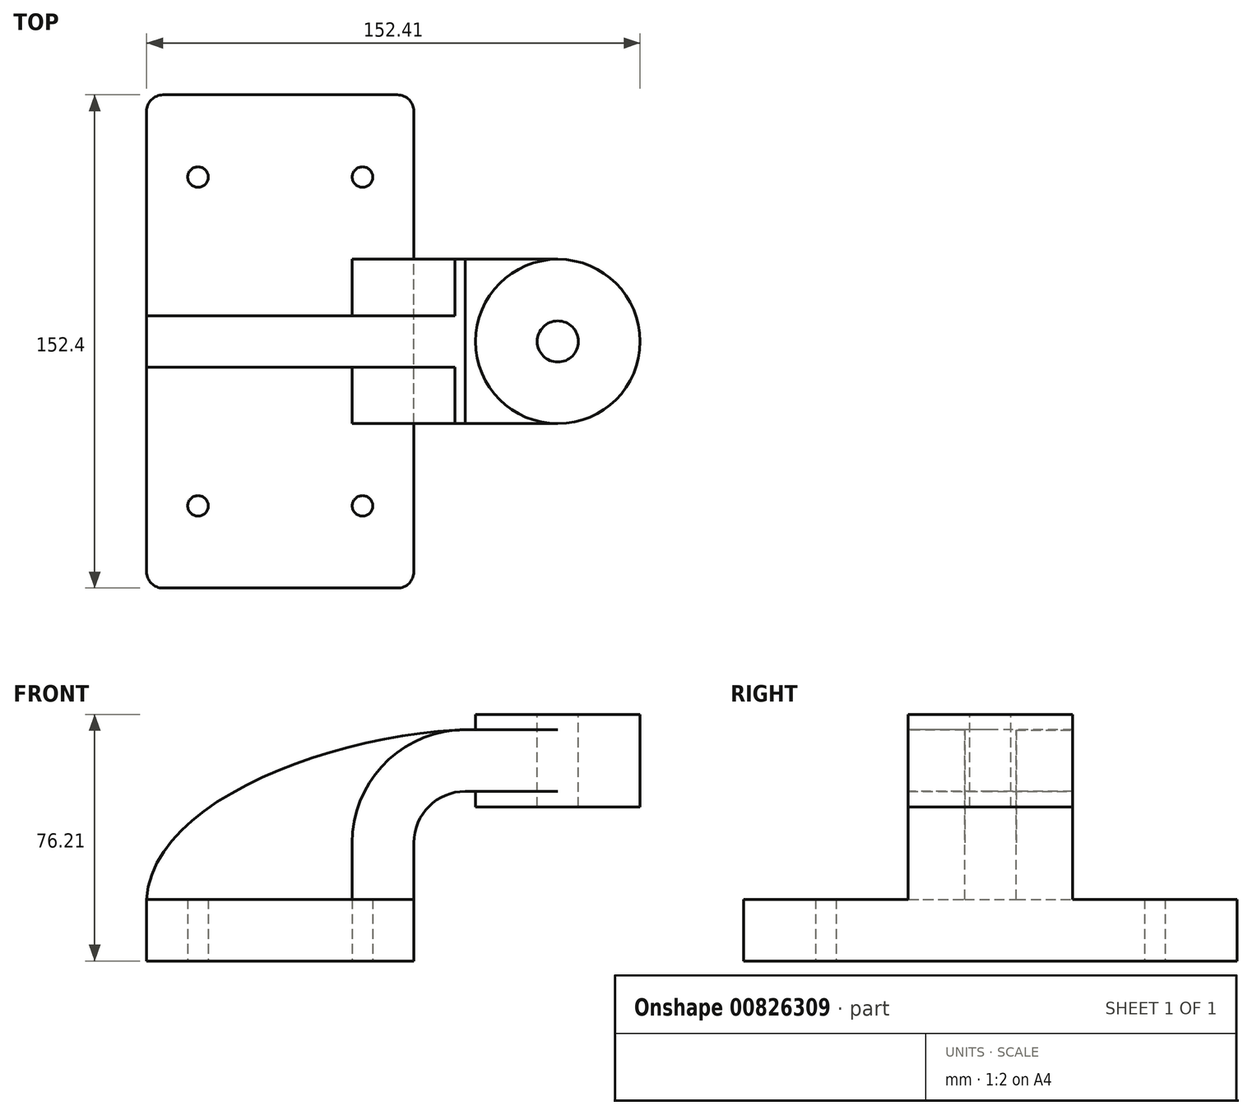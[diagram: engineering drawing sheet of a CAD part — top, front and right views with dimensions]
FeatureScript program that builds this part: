
annotation { "Feature Type Name" : "Feature", "Feature Type Description" : "" }
export const myFeature = defineFeature(function(context is Context, id is Id, definition is map)
    precondition{}
    {
        {
            var Q0;
            Q0=qCreatedBy(makeId("Front.planeOp"),FACE);
            var sketch = newSketch(context, id + "F0", { "sketchPlane" : qUnion([Q0])});
            skLineSegment(sketch, "E0.rect.bottom", {"start": v(-41.28, 9.52) * mm, "end": v(41.28, 9.52) * mm});
            skLineSegment(sketch, "E0.rect.top", {"start": v(-41.28, -9.52) * mm, "end": v(41.28, -9.52) * mm});
            skLineSegment(sketch, "E0.rect.left", {"start": v(-41.28, 9.52) * mm, "end": v(-41.28, -9.52) * mm});
            skLineSegment(sketch, "E0.rect.right", {"start": v(41.28, 9.52) * mm, "end": v(41.28, -9.52) * mm});
            skPoint(sketch, "E0.rect.middle", {"position": v(0, 0) * mm});
            skLineSegment(sketch, "E1", {"start": v(41.28, 9.52) * mm, "end": v(41.28, 27) * mm});
            skArc(sketch, "E2", {"start": v(41.28, 27) * mm, "mid": v(45.92, 38.23) * mm, "end": v(57.15, 42.88) * mm});
            skLineSegment(sketch, "E3", {"start": v(57.15, 42.88) * mm, "end": v(85.72, 42.88) * mm});
            skLineSegment(sketch, "E4.rect.bottom", {"start": v(60.32, 38.1) * mm, "end": v(111.12, 38.1) * mm});
            skLineSegment(sketch, "E4.rect.top", {"start": v(60.32, 66.68) * mm, "end": v(111.12, 66.68) * mm});
            skLineSegment(sketch, "E4.rect.left", {"start": v(60.32, 38.1) * mm, "end": v(60.32, 66.68) * mm});
            skLineSegment(sketch, "E4.rect.right", {"start": v(111.13, 38.1) * mm, "end": v(111.12, 66.68) * mm});
            skPoint(sketch, "E4.rect.middle", {"position": v(85.72, 52.39) * mm});
            skLineSegment(sketch, "E5.0", {"start": v(57.15, 61.93) * mm, "end": v(85.72, 61.93) * mm});
            skArc(sketch, "E5.1", {"start": v(22.23, 27) * mm, "mid": v(32.45, 51.7) * mm, "end": v(57.15, 61.93) * mm});
            skLineSegment(sketch, "E5.2", {"start": v(22.23, 9.52) * mm, "end": v(22.23, 27) * mm});
            skLineSegment(sketch, "E6", {"start": v(85.72, 38.1) * mm, "end": v(85.72, 66.68) * mm});
            skFitSpline(sketch, "E7", {"points": [v(-41.28, 9.53) * mm, v(57.15, 61.93) * mm], "startDerivative": vector(5.2, 92.34) * mm, "endDerivative": vector(120.92, 4.22) * mm});
            skSolve(sketch);
        }
        {
            var Q0;
            Q0=makeQuery(id+"F0.imprint","IMPRINT",FACE,{"disambiguationData":[TD([[makeQuery(id+"F0.imprint","IMPRINT",EDGE,{"derivedFrom":sQuery(id+"F0.wireOp",EDGE,"E0.rect.top")}),1.0]])]});
            extrude(context, id + "F1", {"entities" : qUnion([Q0]), "endBound" : BoundingType.SYMMETRIC, "depth" : 152.4 * mm, "offsetDistance" : 25.4 * mm});
        }
        {
            var Q0;
            {var subQ9=sQuery(id+"F0.wireOp",EDGE,"E1");Q0=makeQuery(id+"F0.imprint","IMPRINT",FACE,{"disambiguationData":[TD([[makeQuery(id+"F0.imprint","IMPRINT",EDGE,{"derivedFrom":subQ9}),1.0]])]});}
            var Q1;
            {var subQ0=sQuery(id+"F0.wireOp",EDGE,"E6");var subQ1=sQuery(id+"F0.wireOp",EDGE,"E3");var subQ2=makeQuery(id+"F0.imprint","INTERSECT",VERTEX,{"derivedFrom":[subQ1,subQ0]});Q1=makeQuery(id+"F0.imprint","IMPRINT",FACE,{"disambiguationData":[TD([[makeQuery(id+"F0.imprint","IMPRINT",EDGE,{"disambiguationData":[TD([[subQ2,1.0]])],"derivedFrom":subQ1}),1.0]])]});}
            extrude(context, id + "F2", {"entities" : qUnion([Q0, Q1]), "operationType" : NewBodyOperationType.ADD, "endBound" : BoundingType.SYMMETRIC, "depth" : 50.8 * mm});
        }
        {
            var Q0;
            {var subQ3=sQuery(id+"F0.wireOp",EDGE,"E5.2");Q0=makeQuery(id+"F0.imprint","IMPRINT",FACE,{"disambiguationData":[TD([[makeQuery(id+"F0.imprint","IMPRINT",EDGE,{"derivedFrom":subQ3}),1.0]])]});}
            extrude(context, id + "F3", {"entities" : qUnion([Q0]), "operationType" : NewBodyOperationType.ADD, "endBound" : BoundingType.SYMMETRIC, "depth" : 15.88 * mm});
        }
        {
            var Q0;
            {var subQ5=sQuery(id+"F0.wireOp",EDGE,"E4.rect.right");Q0=makeQuery(id+"F0.imprint","IMPRINT",FACE,{"disambiguationData":[TD([[makeQuery(id+"F0.imprint","IMPRINT",EDGE,{"derivedFrom":subQ5}),1.0]])]});}
            var Q1;
            Q1=sQuery(id+"F0.wireOp",EDGE,"E6");
            revolve(context, id + "F4", {"operationType" : NewBodyOperationType.ADD, "entities" : qUnion([Q0]), "axis" : qUnion([Q1]), "revolveType" : RevolveType.FULL});
        }
        {
            var Q0;
            Q0=makeQuery(id+"F1.opExtrude","CAP_EDGE",EDGE,{"disambiguationData":[OSD([sQuery(id+"F0.wireOp",EDGE,"E0.rect.right")])],"isStart":false});
            var Q1;
            Q1=makeQuery(id+"F1.opExtrude","CAP_EDGE",EDGE,{"disambiguationData":[OSD([sQuery(id+"F0.wireOp",EDGE,"E0.rect.left")])],"isStart":false});
            var Q2;
            Q2=makeQuery(id+"F1.opExtrude","CAP_EDGE",EDGE,{"disambiguationData":[OSD([sQuery(id+"F0.wireOp",EDGE,"E0.rect.right")])],"isStart":true});
            var Q3;
            Q3=makeQuery(id+"F1.opExtrude","CAP_EDGE",EDGE,{"disambiguationData":[OSD([sQuery(id+"F0.wireOp",EDGE,"E0.rect.left")])],"isStart":true});
            fillet(context, id + "F5", {"entities" : qUnion([Q0, Q1, Q2, Q3]), "radius" : 5.08 * mm, "tangentPropagation" : true, "allowEdgeOverflow" : false});
        }
        {
            var Q0;
            Q0=makeQuery(id+"F4.opRevolve","SWEPT_FACE",FACE,{"disambiguationData":[OSD([sQuery(id+"F0.wireOp",EDGE,"E4.rect.top")])]});
            var sketch = newSketch(context, id + "F6", { "sketchPlane" : qUnion([Q0])});
            skCircle(sketch, "E8", {"center": v(85.72, 0) * mm, "radius": 6.35 * mm});
            skSolve(sketch);
        }
        {
            var Q0;
            Q0 = qSketchRegion(id + "F6", true);
            extrude(context, id + "F7", {"entities" : qUnion([Q0]), "operationType" : NewBodyOperationType.REMOVE, "oppositeDirection" : true, "depth" : 70.61 * mm, "offsetDistance" : 25.4 * mm});
        }
        {
            var Q0;
            Q0=makeQuery(id+"F1.opExtrude","SWEPT_FACE",FACE,{"disambiguationData":[OSD([sQuery(id+"F0.wireOp",EDGE,"E0.rect.top")])]});
            var sketch = newSketch(context, id + "F8", { "sketchPlane" : qUnion([Q0])});
            skCircle(sketch, "E9", {"center": v(25.4, -50.8) * mm, "radius": 3.18 * mm});
            skCircle(sketch, "E10", {"center": v(-25.4, -50.8) * mm, "radius": 3.18 * mm});
            skCircle(sketch, "E11", {"center": v(-25.4, 50.8) * mm, "radius": 3.18 * mm});
            skCircle(sketch, "E12", {"center": v(25.4, 50.8) * mm, "radius": 3.18 * mm});
            skSolve(sketch);
        }
        {
            var Q0;
            Q0 = qSketchRegion(id + "F8", true);
            extrude(context, id + "F9", {"entities" : qUnion([Q0]), "operationType" : NewBodyOperationType.REMOVE, "oppositeDirection" : true, "depth" : 19.05 * mm, "offsetDistance" : 25.4 * mm});
        }
    });
